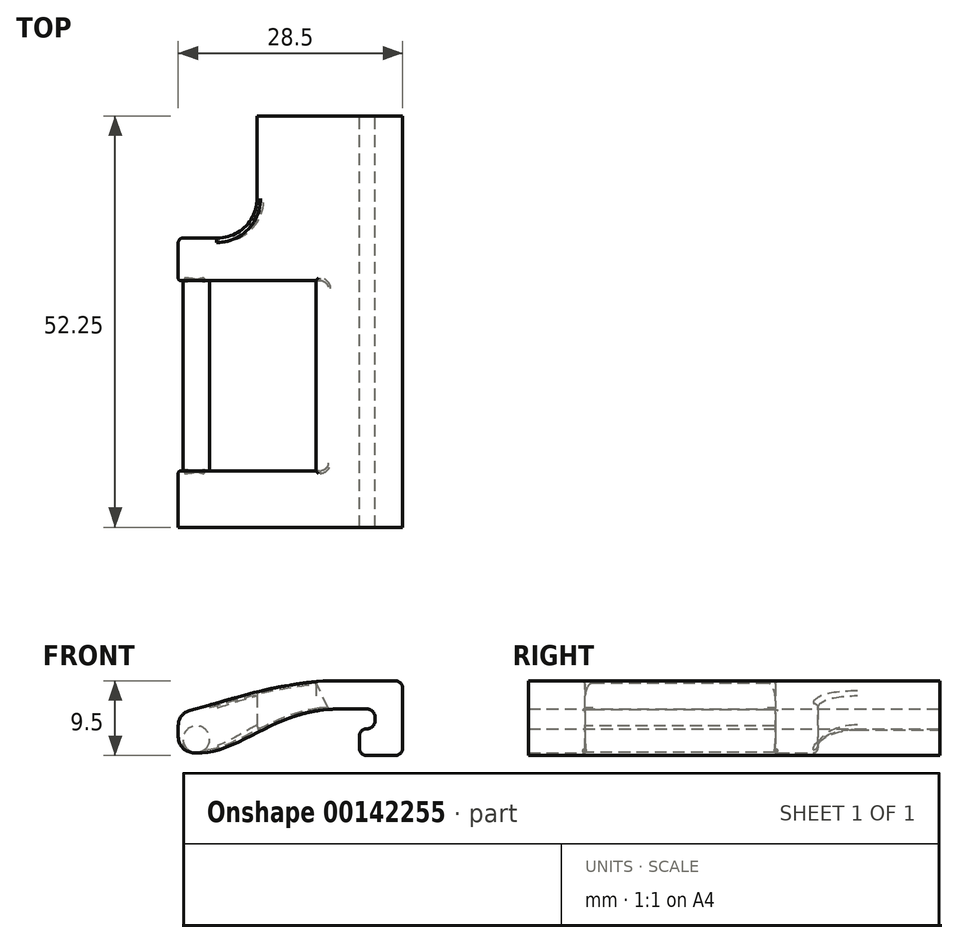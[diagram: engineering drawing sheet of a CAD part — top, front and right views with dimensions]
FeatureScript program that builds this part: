
annotation { "Feature Type Name" : "Feature", "Feature Type Description" : "" }
export const myFeature = defineFeature(function(context is Context, id is Id, definition is map)
    precondition{}
    {
        {
            var Q0;
            Q0=qCreatedBy(makeId("Front.planeOp"),FACE);
            var sketch = newSketch(context, id + "F0", { "sketchPlane" : qUnion([Q0])});
            skLineSegment(sketch, "E0", {"start": v(0, 0) * mm, "end": v(5.5, 0) * mm});
            skLineSegment(sketch, "E1", {"start": v(5.5, 0) * mm, "end": v(5.5, 9.5) * mm});
            skLineSegment(sketch, "E2", {"start": v(5.5, 9.5) * mm, "end": v(-3.5, 9.5) * mm});
            skFitSpline(sketch, "E3", {"points": [v(-3.5, 9.5) * mm, v(-11.77, 8.38) * mm, v(-19.14, 6.39) * mm], "startDerivative": vector(-11.49, 0) * mm, "endDerivative": vector(-15.05, -4.03) * mm});
            skLineSegment(sketch, "E4", {"start": v(-23, 5.35) * mm, "end": v(-23, 0.35) * mm});
            skLineSegment(sketch, "E5", {"start": v(-23, 0.35) * mm, "end": v(-20, 0.35) * mm});
            skFitSpline(sketch, "E6", {"points": [v(-20, 0.35) * mm, v(-9.81, 4.42) * mm, v(-3, 5.9) * mm], "startDerivative": vector(15.9, 0) * mm, "endDerivative": vector(10.05, 0) * mm});
            skLineSegment(sketch, "E7", {"start": v(-3, 5.9) * mm, "end": v(2, 5.9) * mm});
            skLineSegment(sketch, "E8", {"start": v(2, 5.9) * mm, "end": v(2, 3.4) * mm});
            skLineSegment(sketch, "E9", {"start": v(2, 3.4) * mm, "end": v(0, 3.4) * mm});
            skLineSegment(sketch, "E10", {"start": v(0, 3.4) * mm, "end": v(0, 0) * mm});
            skLineSegment(sketch, "E11", {"start": v(-23, 5.35) * mm, "end": v(-19.14, 6.39) * mm});
            skSolve(sketch);
        }
        {
            var Q0;
            Q0=makeQuery(id+"F0.imprint","IMPRINT",FACE,{"disambiguationData":[TD([[makeQuery(id+"F0.imprint","IMPRINT",EDGE,{"derivedFrom":sQuery(id+"F0.wireOp",EDGE,"E0")}),1.0]])]});
            extrude(context, id + "F1", {"entities" : qUnion([Q0]), "endBound" : BoundingType.SYMMETRIC, "depth" : 66 * mm});
        }
        {
            var Q0;
            {var subQ0=sQuery(id+"F0.wireOp",EDGE,"E4");var subQ1=sQuery(id+"F0.wireOp",EDGE,"E3");Q0=makeQuery(id+"F4.boolean.opBoolean","SPLIT",EDGE,{"disambiguationData":[TD([makeQuery(id+"F4.opExtrude","CAP_FACE",FACE,{"disambiguationData":[OSD([sQuery(id+"F3.wireOp",EDGE,"E12.bottom"),sQuery(id+"F3.wireOp",EDGE,"E12.top"),sQuery(id+"F3.wireOp",EDGE,"E12.left"),sQuery(id+"F3.wireOp",EDGE,"E12.right")])],"isStart":false})])],"derivedFrom":makeQuery(id+"F1.opExtrude","SWEPT_EDGE",EDGE,{"disambiguationData":[OSD([subQ1,subQ0])]})});}
            var Q1;
            {var subQ0=sQuery(id+"F0.wireOp",EDGE,"E5");var subQ1=sQuery(id+"F0.wireOp",EDGE,"E4");Q1=makeQuery(id+"F4.boolean.opBoolean","SPLIT",EDGE,{"disambiguationData":[TD([makeQuery(id+"F4.opExtrude","CAP_FACE",FACE,{"disambiguationData":[OSD([sQuery(id+"F3.wireOp",EDGE,"E12.bottom"),sQuery(id+"F3.wireOp",EDGE,"E12.top"),sQuery(id+"F3.wireOp",EDGE,"E12.left"),sQuery(id+"F3.wireOp",EDGE,"E12.right")])],"isStart":false})])],"derivedFrom":makeQuery(id+"F1.opExtrude","SWEPT_EDGE",EDGE,{"disambiguationData":[OSD([subQ1,subQ0])]})});}
            fillet(context, id + "F2", {"entities" : qUnion([Q0, Q1]), "radius" : 2 * mm, "tangentPropagation" : true, "allowEdgeOverflow" : false});
        }
        {
            var Q0;
            Q0=qCreatedBy(makeId("Front.planeOp"),FACE);
            var sketch = newSketch(context, id + "F3", { "sketchPlane" : qUnion([Q0])});
            skLineSegment(sketch, "E12.bottom", {"start": v(-23, 12.42) * mm, "end": v(-5.5, 12.42) * mm});
            skLineSegment(sketch, "E12.top", {"start": v(-23, -8) * mm, "end": v(-5.5, -8) * mm});
            skLineSegment(sketch, "E12.left", {"start": v(-23, 12.42) * mm, "end": v(-23, -8) * mm});
            skLineSegment(sketch, "E12.right", {"start": v(-5.5, 12.42) * mm, "end": v(-5.5, -8) * mm});
            skSolve(sketch);
        }
        {
            var Q0;
            Q0=makeQuery(id+"F3.imprint","IMPRINT",FACE,{"disambiguationData":[TD([[makeQuery(id+"F3.imprint","IMPRINT",EDGE,{"derivedFrom":sQuery(id+"F3.wireOp",EDGE,"E12.bottom")}),-1.0]])]});
            extrude(context, id + "F4", {"entities" : qUnion([Q0]), "operationType" : NewBodyOperationType.REMOVE, "endBound" : BoundingType.SYMMETRIC, "depth" : 24.2 * mm});
        }
        {
            var Q0;
            Q0=makeQuery(id+"F1.opExtrude","CAP_FACE",FACE,{"disambiguationData":[OSD([sQuery(id+"F0.wireOp",EDGE,"E0"),sQuery(id+"F0.wireOp",EDGE,"E1"),sQuery(id+"F0.wireOp",EDGE,"E2"),sQuery(id+"F0.wireOp",EDGE,"E3"),sQuery(id+"F0.wireOp",EDGE,"E4"),sQuery(id+"F0.wireOp",EDGE,"E5"),sQuery(id+"F0.wireOp",EDGE,"E6"),sQuery(id+"F0.wireOp",EDGE,"E7"),sQuery(id+"F0.wireOp",EDGE,"E8"),sQuery(id+"F0.wireOp",EDGE,"E9"),sQuery(id+"F0.wireOp",EDGE,"E10")])],"isStart":false});
            var sketch = newSketch(context, id + "F5", { "sketchPlane" : qUnion([Q0])});
            skCircle(sketch, "E13", {"center": v(-20.7, 2.07) * mm, "radius": 1.7 * mm});
            skSolve(sketch);
        }
        {
            var Q0;
            Q0=makeQuery(id+"F4.boolean.opBoolean","INTERSECT",EDGE,{"derivedFrom":[makeQuery(id+"F1.opExtrude","SWEPT_FACE",FACE,{"disambiguationData":[OSD([sQuery(id+"F0.wireOp",EDGE,"E6")])]}),makeQuery(id+"F4.opExtrude","SWEPT_FACE",FACE,{"disambiguationData":[OSD([sQuery(id+"F3.wireOp",EDGE,"E12.right")])]})]});
            chamfer(context, id + "F6", {"entities" : qUnion([Q0]), "chamferType" : ChamferType.TWO_OFFSETS, "width1" : 2 * mm, "oppositeDirection" : false, "width2" : 3.7 * mm, "tangentPropagation" : true});
        }
        {
            var Q0;
            {var subQ0=sQuery(id+"F3.wireOp",EDGE,"E12.right");Q0=makeQuery(id+"F6.opChamfer","BLEND_EDGE",EDGE,{"blendedFrom":[makeQuery(id+"F4.boolean.opBoolean","INTERSECT",EDGE,{"derivedFrom":[makeQuery(id+"F1.opExtrude","SWEPT_FACE",FACE,{"disambiguationData":[OSD([sQuery(id+"F0.wireOp",EDGE,"E6")])]}),makeQuery(id+"F4.opExtrude","SWEPT_FACE",FACE,{"disambiguationData":[OSD([subQ0])]})]}),makeQuery(id+"F4.boolean.opBoolean","COPY",FACE,{"derivedFrom":makeQuery(id+"F4.opExtrude","CAP_FACE",FACE,{"disambiguationData":[OSD([sQuery(id+"F3.wireOp",EDGE,"E12.bottom"),sQuery(id+"F3.wireOp",EDGE,"E12.top"),sQuery(id+"F3.wireOp",EDGE,"E12.left"),subQ0])],"isStart":true})})],"blendedInto":[makeQuery(id+"F4.boolean.opBoolean","COPY",FACE,{"derivedFrom":makeQuery(id+"F4.opExtrude","CAP_FACE",FACE,{"disambiguationData":[OSD([sQuery(id+"F3.wireOp",EDGE,"E12.bottom"),sQuery(id+"F3.wireOp",EDGE,"E12.top"),sQuery(id+"F3.wireOp",EDGE,"E12.left"),subQ0])],"isStart":true})})]});}
            var Q1;
            {var subQ0=sQuery(id+"F3.wireOp",EDGE,"E12.right");Q1=makeQuery(id+"F6.opChamfer","BLEND_EDGE",EDGE,{"blendedFrom":[makeQuery(id+"F4.boolean.opBoolean","INTERSECT",EDGE,{"derivedFrom":[makeQuery(id+"F1.opExtrude","SWEPT_FACE",FACE,{"disambiguationData":[OSD([sQuery(id+"F0.wireOp",EDGE,"E6")])]}),makeQuery(id+"F4.opExtrude","SWEPT_FACE",FACE,{"disambiguationData":[OSD([subQ0])]})]}),makeQuery(id+"F4.boolean.opBoolean","COPY",FACE,{"derivedFrom":makeQuery(id+"F4.opExtrude","CAP_FACE",FACE,{"disambiguationData":[OSD([sQuery(id+"F3.wireOp",EDGE,"E12.bottom"),sQuery(id+"F3.wireOp",EDGE,"E12.top"),sQuery(id+"F3.wireOp",EDGE,"E12.left"),subQ0])],"isStart":false})})],"blendedInto":[makeQuery(id+"F4.boolean.opBoolean","COPY",FACE,{"derivedFrom":makeQuery(id+"F4.opExtrude","CAP_FACE",FACE,{"disambiguationData":[OSD([sQuery(id+"F3.wireOp",EDGE,"E12.bottom"),sQuery(id+"F3.wireOp",EDGE,"E12.top"),sQuery(id+"F3.wireOp",EDGE,"E12.left"),subQ0])],"isStart":false})})]});}
            fillet(context, id + "F7", {"entities" : qUnion([Q0, Q1]), "radius" : 1 * mm, "tangentPropagation" : true, "allowEdgeOverflow" : false});
        }
        {
            var Q0;
            Q0 = qSketchRegion(id + "F5", true);
            var Q1;
            Q1=makeQuery(id+"F1.opExtrude","CAP_FACE",FACE,{"disambiguationData":[OSD([sQuery(id+"F0.wireOp",EDGE,"E0"),sQuery(id+"F0.wireOp",EDGE,"E1"),sQuery(id+"F0.wireOp",EDGE,"E2"),sQuery(id+"F0.wireOp",EDGE,"E3"),sQuery(id+"F0.wireOp",EDGE,"E4"),sQuery(id+"F0.wireOp",EDGE,"E5"),sQuery(id+"F0.wireOp",EDGE,"E6"),sQuery(id+"F0.wireOp",EDGE,"E7"),sQuery(id+"F0.wireOp",EDGE,"E8"),sQuery(id+"F0.wireOp",EDGE,"E9"),sQuery(id+"F0.wireOp",EDGE,"E10")])],"isStart":true});
            extrude(context, id + "F8", {"entities" : qUnion([Q0]), "operationType" : NewBodyOperationType.ADD, "endBound" : BoundingType.UP_TO_SURFACE, "oppositeDirection" : true, "endBoundEntityFace" : qUnion([Q1]), "depth" : 25 * mm});
        }
        {
            var Q0;
            Q0=makeQuery(id+"F1.opExtrude","CAP_FACE",FACE,{"disambiguationData":[OSD([sQuery(id+"F0.wireOp",EDGE,"E0"),sQuery(id+"F0.wireOp",EDGE,"E1"),sQuery(id+"F0.wireOp",EDGE,"E2"),sQuery(id+"F0.wireOp",EDGE,"E3"),sQuery(id+"F0.wireOp",EDGE,"E4"),sQuery(id+"F0.wireOp",EDGE,"E5"),sQuery(id+"F0.wireOp",EDGE,"E6"),sQuery(id+"F0.wireOp",EDGE,"E7"),sQuery(id+"F0.wireOp",EDGE,"E8"),sQuery(id+"F0.wireOp",EDGE,"E9"),sQuery(id+"F0.wireOp",EDGE,"E10")])],"isStart":false});
            extrude(context, id + "F9", {"entities" : qUnion([Q0]), "operationType" : NewBodyOperationType.REMOVE, "oppositeDirection" : true, "depth" : 13.75 * mm});
        }
        {
            var Q0;
            Q0=makeQuery(id+"F1.opExtrude","SWEPT_EDGE",EDGE,{"disambiguationData":[OSD([sQuery(id+"F0.wireOp",EDGE,"E9"),sQuery(id+"F0.wireOp",EDGE,"E10")])]});
            var Q1;
            Q1=makeQuery(id+"F1.opExtrude","SWEPT_EDGE",EDGE,{"disambiguationData":[OSD([sQuery(id+"F0.wireOp",EDGE,"E0"),sQuery(id+"F0.wireOp",EDGE,"E10")])]});
            var Q2;
            Q2=makeQuery(id+"F1.opExtrude","SWEPT_EDGE",EDGE,{"disambiguationData":[OSD([sQuery(id+"F0.wireOp",EDGE,"E8"),sQuery(id+"F0.wireOp",EDGE,"E9")])]});
            var Q3;
            Q3=makeQuery(id+"F1.opExtrude","SWEPT_EDGE",EDGE,{"disambiguationData":[OSD([sQuery(id+"F0.wireOp",EDGE,"E7"),sQuery(id+"F0.wireOp",EDGE,"E8")])]});
            var Q4;
            Q4=makeQuery(id+"F1.opExtrude","SWEPT_EDGE",EDGE,{"disambiguationData":[OSD([sQuery(id+"F0.wireOp",EDGE,"E0"),sQuery(id+"F0.wireOp",EDGE,"E1")])]});
            var Q5;
            Q5=makeQuery(id+"F1.opExtrude","SWEPT_EDGE",EDGE,{"disambiguationData":[OSD([sQuery(id+"F0.wireOp",EDGE,"E1"),sQuery(id+"F0.wireOp",EDGE,"E2")])]});
            fillet(context, id + "F10", {"entities" : qUnion([Q0, Q1, Q2, Q3, Q4, Q5]), "radius" : 1 * mm, "tangentPropagation" : true, "allowEdgeOverflow" : false});
        }
        {
            var Q0;
            Q0=qCreatedBy(makeId("Top.planeOp"),FACE);
            var sketch = newSketch(context, id + "F11", { "sketchPlane" : qUnion([Q0])});
            skLineSegment(sketch, "E14.bottom", {"start": v(-23, 33) * mm, "end": v(-13, 33) * mm});
            skLineSegment(sketch, "E14.top", {"start": v(-23, 17.5) * mm, "end": v(-13, 17.5) * mm});
            skLineSegment(sketch, "E14.left", {"start": v(-23, 33) * mm, "end": v(-23, 17.5) * mm});
            skLineSegment(sketch, "E14.right", {"start": v(-13, 33) * mm, "end": v(-13, 17.5) * mm});
            skSolve(sketch);
        }
        {
            var Q0;
            Q0 = qSketchRegion(id + "F11", true);
            extrude(context, id + "F12", {"entities" : qUnion([Q0]), "operationType" : NewBodyOperationType.REMOVE, "depth" : 25 * mm});
        }
        {
            var Q0;
            Q0=makeQuery(id+"F12.boolean.opBoolean","COPY",EDGE,{"derivedFrom":makeQuery(id+"F12.opExtrude","SWEPT_EDGE",EDGE,{"disambiguationData":[OSD([sQuery(id+"F11.wireOp",EDGE,"E14.bottom"),sQuery(id+"F11.wireOp",EDGE,"E14.right")])]})});
            var Q1;
            Q1=makeQuery(id+"F12.boolean.opBoolean","COPY",EDGE,{"derivedFrom":makeQuery(id+"F12.opExtrude","SWEPT_EDGE",EDGE,{"disambiguationData":[OSD([sQuery(id+"F11.wireOp",EDGE,"E14.top"),sQuery(id+"F11.wireOp",EDGE,"E14.right")])]})});
            fillet(context, id + "F13", {"entities" : qUnion([Q0, Q1]), "radius" : 5 * mm, "tangentPropagation" : true, "allowEdgeOverflow" : false});
        }
        {
            var Q0;
            Q0=makeQuery(id+"F9.boolean.opBoolean","COPY",EDGE,{"derivedFrom":makeQuery(id+"F9.opExtrude","CAP_EDGE",EDGE,{"disambiguationData":[OSD([sQuery(id+"F0.wireOp",EDGE,"E3")])],"isStart":false})});
            var Q1;
            Q1=makeQuery(id+"F12.boolean.opBoolean","INTERSECT",EDGE,{"derivedFrom":[makeQuery(id+"F1.opExtrude","SWEPT_FACE",FACE,{"disambiguationData":[OSD([sQuery(id+"F0.wireOp",EDGE,"E3")])]}),makeQuery(id+"F12.opExtrude","SWEPT_FACE",FACE,{"disambiguationData":[OSD([sQuery(id+"F11.wireOp",EDGE,"E14.top")])]})]});
            fillet(context, id + "F14", {"entities" : qUnion([Q0, Q1]), "radius" : 0.6 * mm, "tangentPropagation" : true, "allowEdgeOverflow" : false});
        }
        {
            var Q0;
            Q0=makeQuery(id+"F4.boolean.opBoolean","INTERSECT",EDGE,{"derivedFrom":[makeQuery(id+"F1.opExtrude","SWEPT_FACE",FACE,{"disambiguationData":[OSD([sQuery(id+"F0.wireOp",EDGE,"E3")])]}),makeQuery(id+"F4.opExtrude","SWEPT_FACE",FACE,{"disambiguationData":[OSD([sQuery(id+"F3.wireOp",EDGE,"E12.right")])]})]});
            var Q1;
            Q1=makeQuery(id+"F4.boolean.opBoolean","INTERSECT",EDGE,{"derivedFrom":[makeQuery(id+"F1.opExtrude","SWEPT_FACE",FACE,{"disambiguationData":[OSD([sQuery(id+"F0.wireOp",EDGE,"E3")])]}),makeQuery(id+"F4.opExtrude","CAP_FACE",FACE,{"disambiguationData":[OSD([sQuery(id+"F3.wireOp",EDGE,"E12.bottom"),sQuery(id+"F3.wireOp",EDGE,"E12.top"),sQuery(id+"F3.wireOp",EDGE,"E12.left"),sQuery(id+"F3.wireOp",EDGE,"E12.right")])],"isStart":true})]});
            var Q2;
            Q2=makeQuery(id+"F4.boolean.opBoolean","INTERSECT",EDGE,{"derivedFrom":[makeQuery(id+"F1.opExtrude","SWEPT_FACE",FACE,{"disambiguationData":[OSD([sQuery(id+"F0.wireOp",EDGE,"E3")])]}),makeQuery(id+"F4.opExtrude","CAP_FACE",FACE,{"disambiguationData":[OSD([sQuery(id+"F3.wireOp",EDGE,"E12.bottom"),sQuery(id+"F3.wireOp",EDGE,"E12.top"),sQuery(id+"F3.wireOp",EDGE,"E12.left"),sQuery(id+"F3.wireOp",EDGE,"E12.right")])],"isStart":false})]});
            fillet(context, id + "F15", {"entities" : qUnion([Q0, Q1, Q2]), "radius" : 0.3 * mm, "tangentPropagation" : true, "allowEdgeOverflow" : false});
        }
        {
            var Q0;
            Q0=makeQuery(id+"F8.boolean.opBoolean","INTERSECT",EDGE,{"derivedFrom":[makeQuery(id+"F4.boolean.opBoolean","COPY",FACE,{"derivedFrom":makeQuery(id+"F4.opExtrude","CAP_FACE",FACE,{"disambiguationData":[OSD([sQuery(id+"F3.wireOp",EDGE,"E12.bottom"),sQuery(id+"F3.wireOp",EDGE,"E12.top"),sQuery(id+"F3.wireOp",EDGE,"E12.left"),sQuery(id+"F3.wireOp",EDGE,"E12.right")])],"isStart":true})}),makeQuery(id+"F8.opExtrude","SWEPT_FACE",FACE,{"disambiguationData":[OSD([sQuery(id+"F5.wireOp",EDGE,"E13")])]})]});
            var Q1;
            Q1=makeQuery(id+"F8.boolean.opBoolean","INTERSECT",EDGE,{"derivedFrom":[makeQuery(id+"F4.boolean.opBoolean","COPY",FACE,{"derivedFrom":makeQuery(id+"F4.opExtrude","CAP_FACE",FACE,{"disambiguationData":[OSD([sQuery(id+"F3.wireOp",EDGE,"E12.bottom"),sQuery(id+"F3.wireOp",EDGE,"E12.top"),sQuery(id+"F3.wireOp",EDGE,"E12.left"),sQuery(id+"F3.wireOp",EDGE,"E12.right")])],"isStart":false})}),makeQuery(id+"F8.opExtrude","SWEPT_FACE",FACE,{"disambiguationData":[OSD([sQuery(id+"F5.wireOp",EDGE,"E13")])]})]});
            fillet(context, id + "F16", {"entities" : qUnion([Q0, Q1]), "radius" : 0.15 * mm, "tangentPropagation" : true, "allowEdgeOverflow" : false});
        }
    });
